# Revit family: 6121 TARO Dining Table
name_source: partatom
category: Furniture
revit_build: Autodesk Revit 2017 (Build: 20171027_0315(x64)
units: mm (PartAtom-declared; Revit-internal decimal feet)

## family parameters
Always vertical = Yes
Cut with Voids When Loaded = No
OmniClass Number = 23.40.20.00
OmniClass Title = General Furniture and Specialties
Room Calculation Point = No
Shared = No
Work Plane-Based = No

## types (1)
- 6121 TARO Dining Table
    Description = Taro is a series of solid oak tables created with a strong focus on daily function and use, whether in the kitchen, dining area or meeting room. With machined grooves along its length, the table top resembles a traditional plank table, but has been executed in a refined and knotless selection of oak that will acquire the most beautiful patina.
    Design year = 2016
    Diameter = 120 cm
    Frame = FF Oak Smoked horizontal
    Height = 73 cm
    Item No. = 6121
    Legs = FF Oak Smoked vertical
    Manufacturer = Fredericia Furniture
    Model = TARO Dining Table
    Table Top = FF Oak Smoked horizontal
    URL = https://www.fredericia.com
    Variation Frame - Extra charge = Available in other kinds of wood
    Variation Frame - Standard = Available in other kinds of wood
    Variations - Extra charge = Table with milled groves
    Weight = 41,5 kg

## geometry (parser evidence)
native form markers: Sweep x3
no freeform markers — native parametric forms only
